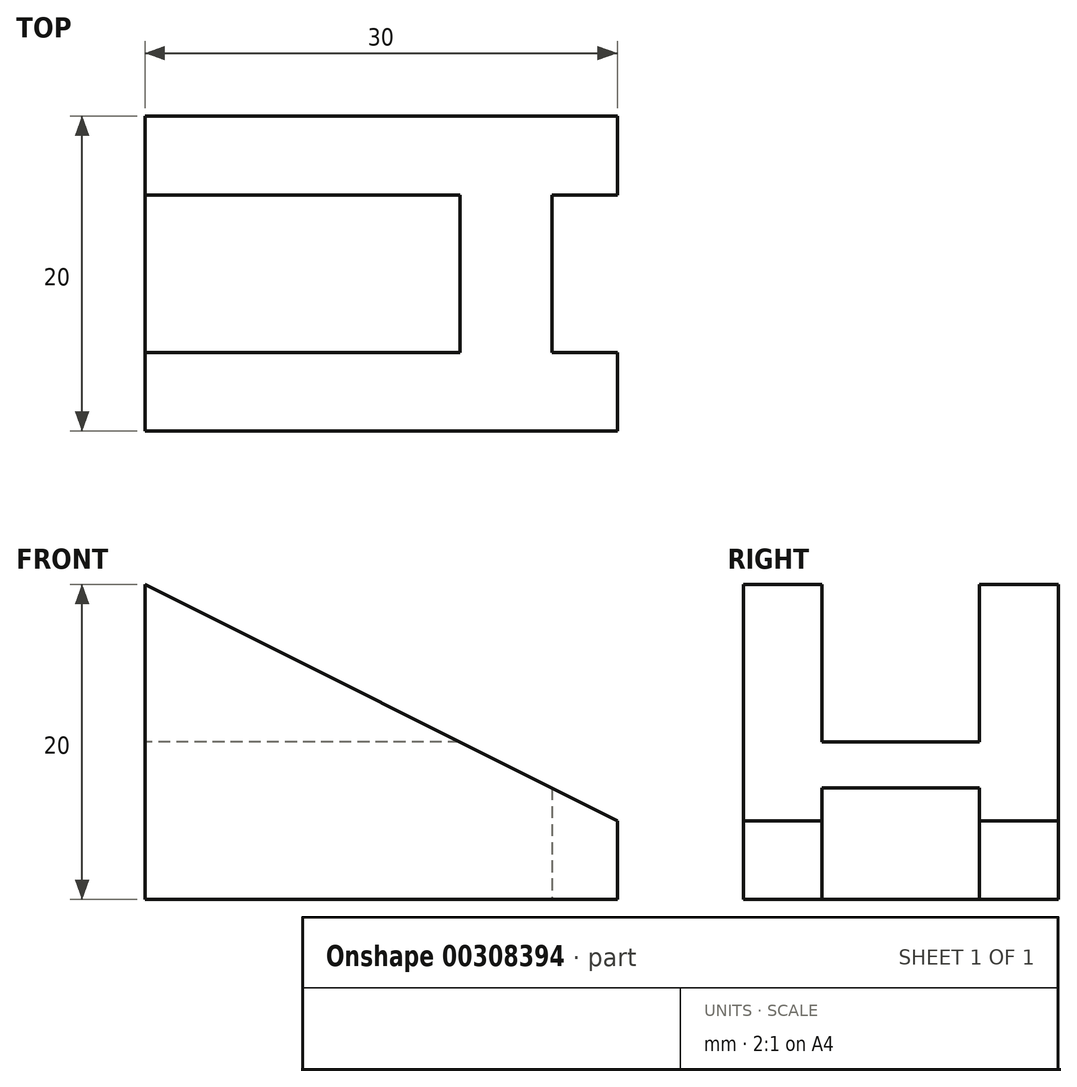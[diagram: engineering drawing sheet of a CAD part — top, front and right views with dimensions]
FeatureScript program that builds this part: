
annotation { "Feature Type Name" : "Feature", "Feature Type Description" : "" }
export const myFeature = defineFeature(function(context is Context, id is Id, definition is map)
    precondition{}
    {
        {
            var Q0;
            Q0=qCreatedBy(makeId("Front.planeOp"),FACE);
            var sketch = newSketch(context, id + "F0", { "sketchPlane" : qUnion([Q0])});
            skLineSegment(sketch, "E0", {"start": v(0, 0) * mm, "end": v(0, 20) * mm});
            skLineSegment(sketch, "E1", {"start": v(0, 20) * mm, "end": v(0, 0) * mm});
            skLineSegment(sketch, "E2", {"start": v(30, 0) * mm, "end": v(30, 5) * mm});
            skLineSegment(sketch, "E3", {"start": v(30, 5) * mm, "end": v(0, 20) * mm});
            skLineSegment(sketch, "E4", {"start": v(0, 0) * mm, "end": v(30, 0) * mm});
            skSolve(sketch);
        }
        {
            var Q0;
            Q0 = qSketchRegion(id + "F0", true);
            extrude(context, id + "F1", {"entities" : qUnion([Q0]), "oppositeDirection" : true, "depth" : 20 * mm});
        }
        {
            var Q0;
            Q0=qCreatedBy(makeId("Right.planeOp"),FACE);
            var sketch = newSketch(context, id + "F2", { "sketchPlane" : qUnion([Q0])});
            skLineSegment(sketch, "E5", {"start": v(5, 20) * mm, "end": v(0, 20) * mm});
            skLineSegment(sketch, "E6", {"start": v(20, 20) * mm, "end": v(15, 20) * mm});
            skLineSegment(sketch, "E7", {"start": v(5, 20) * mm, "end": v(5, 10) * mm});
            skLineSegment(sketch, "E8", {"start": v(15, 20) * mm, "end": v(15, 10) * mm});
            skLineSegment(sketch, "E9", {"start": v(15, 10) * mm, "end": v(5, 10) * mm});
            skLineSegment(sketch, "E10", {"start": v(5, 20) * mm, "end": v(15, 20) * mm});
            skSolve(sketch);
        }
        {
            var Q0;
            Q0 = qSketchRegion(id + "F2", true);
            extrude(context, id + "F3", {"entities" : qUnion([Q0]), "operationType" : NewBodyOperationType.REMOVE, "depth" : 25 * mm});
        }
        {
            var Q0;
            Q0=qCreatedBy(makeId("Top.planeOp"),FACE);
            var sketch = newSketch(context, id + "F4", { "sketchPlane" : qUnion([Q0])});
            skLineSegment(sketch, "E11", {"start": v(30, 20) * mm, "end": v(30, 15) * mm});
            skLineSegment(sketch, "E12", {"start": v(30, 0) * mm, "end": v(30, 5) * mm});
            skLineSegment(sketch, "E13", {"start": v(30, 15) * mm, "end": v(25.86, 15) * mm});
            skLineSegment(sketch, "E14", {"start": v(25.86, 15) * mm, "end": v(25.86, 5) * mm});
            skLineSegment(sketch, "E15", {"start": v(25.86, 5) * mm, "end": v(30, 5) * mm});
            skLineSegment(sketch, "E16", {"start": v(30, 15) * mm, "end": v(30, 5) * mm});
            skSolve(sketch);
        }
        {
            var Q0;
            Q0 = qSketchRegion(id + "F4", true);
            extrude(context, id + "F5", {"entities" : qUnion([Q0]), "operationType" : NewBodyOperationType.REMOVE, "depth" : 25 * mm});
        }
    });
